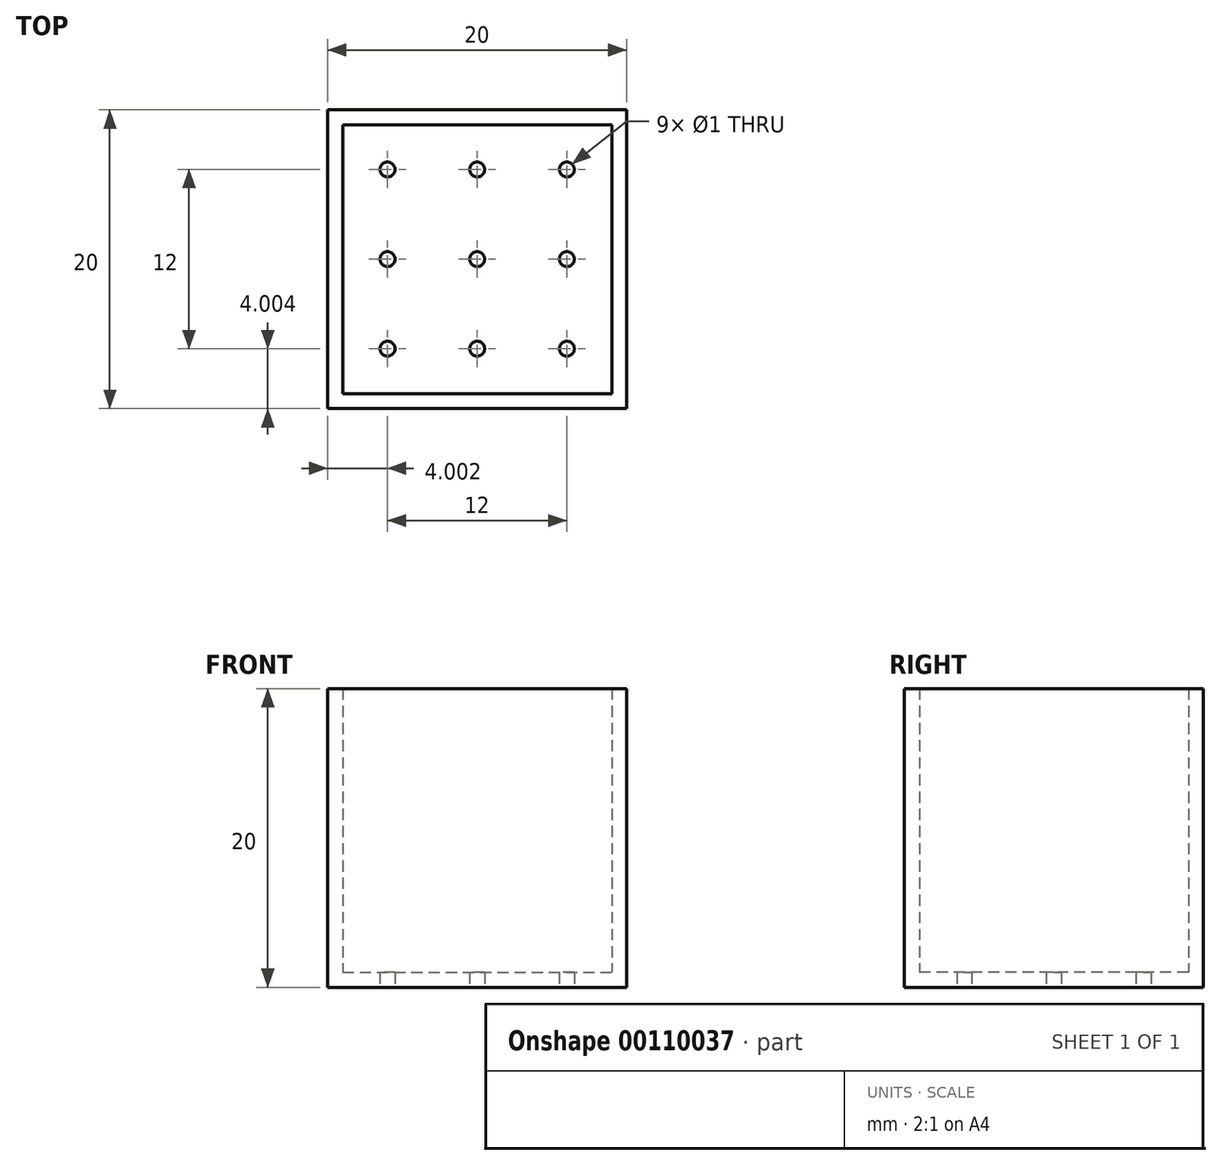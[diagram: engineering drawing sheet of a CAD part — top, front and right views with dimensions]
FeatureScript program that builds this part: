
annotation { "Feature Type Name" : "Feature", "Feature Type Description" : "" }
export const myFeature = defineFeature(function(context is Context, id is Id, definition is map)
    precondition{}
    {
        {
            var Q0;
            Q0=qCreatedBy(makeId("Top.planeOp"),FACE);
            var sketch = newSketch(context, id + "F0", { "sketchPlane" : qUnion([Q0])});
            skLineSegment(sketch, "E0.bottom", {"start": v(-1.53, -6.57) * mm, "end": v(18.47, -6.57) * mm});
            skLineSegment(sketch, "E0.top", {"start": v(-1.53, -26.57) * mm, "end": v(18.47, -26.57) * mm});
            skLineSegment(sketch, "E0.left", {"start": v(-1.53, -6.57) * mm, "end": v(-1.53, -26.57) * mm});
            skLineSegment(sketch, "E0.right", {"start": v(18.47, -6.57) * mm, "end": v(18.47, -26.57) * mm});
            skSolve(sketch);
        }
        {
            var Q0;
            Q0 = qSketchRegion(id + "F0", true);
            extrude(context, id + "F1", {"entities" : qUnion([Q0]), "depth" : 20 * mm});
        }
        {
            var Q0;
            Q0=makeQuery(id+"F1.opExtrude","CAP_FACE",FACE,{"disambiguationData":[OSD([sQuery(id+"F0.wireOp",EDGE,"E0.bottom"),sQuery(id+"F0.wireOp",EDGE,"E0.top"),sQuery(id+"F0.wireOp",EDGE,"E0.left"),sQuery(id+"F0.wireOp",EDGE,"E0.right")])],"isStart":false});
            shell(context, id + "F2", {"entities" : qUnion([Q0]), "thickness" : 1 * mm});
        }
        {
            var Q0;
            Q0=makeQuery(id+"F1.opExtrude","CAP_FACE",FACE,{"disambiguationData":[OSD([sQuery(id+"F0.wireOp",EDGE,"E0.bottom"),sQuery(id+"F0.wireOp",EDGE,"E0.top"),sQuery(id+"F0.wireOp",EDGE,"E0.left"),sQuery(id+"F0.wireOp",EDGE,"E0.right")])],"isStart":true});
            var sketch = newSketch(context, id + "F3", { "sketchPlane" : qUnion([Q0])});
            skPoint(sketch, "E1", {"position": v(2.47, 22.57) * mm});
            skPoint(sketch, "E2.0.1.0", {"position": v(2.47, 16.57) * mm});
            skPoint(sketch, "E2.0.2.0", {"position": v(2.47, 10.57) * mm});
            skPoint(sketch, "E2.1.0.0", {"position": v(8.47, 22.57) * mm});
            skPoint(sketch, "E2.1.1.0", {"position": v(8.47, 16.57) * mm});
            skPoint(sketch, "E2.1.2.0", {"position": v(8.47, 10.57) * mm});
            skPoint(sketch, "E2.2.0.0", {"position": v(14.47, 22.57) * mm});
            skPoint(sketch, "E2.2.1.0", {"position": v(14.47, 16.57) * mm});
            skPoint(sketch, "E2.2.2.0", {"position": v(14.47, 10.57) * mm});
            skLineSegment(sketch, "E2.direction1", {"start": v(2.47, 22.57) * mm, "end": v(8.47, 22.57) * mm, "construction": true});
            skLineSegment(sketch, "E2.direction2", {"start": v(2.47, 22.57) * mm, "end": v(2.47, 16.57) * mm, "construction": true});
            skSolve(sketch);
        }
        {
            var Q0;
            Q0=sQuery(id+"F3.wireOp",VERTEX,"E2.2.2.0");
            var Q1;
            Q1=sQuery(id+"F3.wireOp",VERTEX,"E2.1.2.0");
            var Q2;
            Q2=sQuery(id+"F3.wireOp",VERTEX,"E2.0.2.0");
            var Q3;
            Q3=sQuery(id+"F3.wireOp",VERTEX,"E2.0.1.0");
            var Q4;
            Q4=sQuery(id+"F3.wireOp",VERTEX,"E2.1.1.0");
            var Q5;
            Q5=sQuery(id+"F3.wireOp",VERTEX,"E2.2.1.0");
            var Q6;
            Q6=sQuery(id+"F3.wireOp",VERTEX,"E2.2.0.0");
            var Q7;
            Q7=sQuery(id+"F3.wireOp",VERTEX,"E2.1.0.0");
            var Q8;
            Q8=sQuery(id+"F3.wireOp",VERTEX,"E1");
            var Q9;
            Q9=makeQuery(id+"F1.opExtrude","SWEPT_BODY",BODY,{"disambiguationData":[OSD([sQuery(id+"F0.wireOp",EDGE,"E0.bottom"),sQuery(id+"F0.wireOp",EDGE,"E0.top"),sQuery(id+"F0.wireOp",EDGE,"E0.left"),sQuery(id+"F0.wireOp",EDGE,"E0.right")])]});
            hole(context, id + "F4", {"style" : HoleStyle.SIMPLE, "endStyle" : HoleEndStyle.THROUGH, "holeDiameter" : 1 * mm, "locations" : qUnion([Q0, Q1, Q2, Q3, Q4, Q5, Q6, Q7, Q8]), "scope" : qUnion([Q9]), "isTappedThrough" : true});
        }
    });
